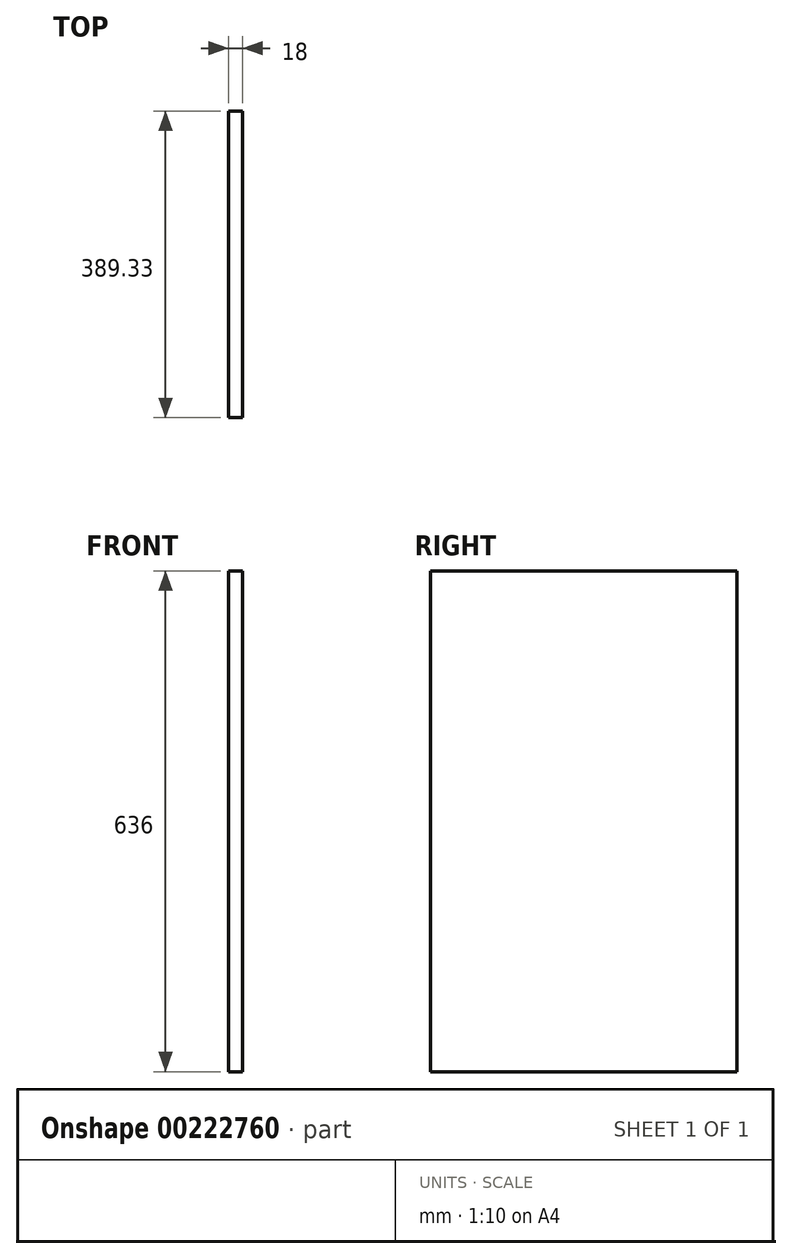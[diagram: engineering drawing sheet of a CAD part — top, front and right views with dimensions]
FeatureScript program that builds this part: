
annotation { "Feature Type Name" : "Feature", "Feature Type Description" : "" }
export const myFeature = defineFeature(function(context is Context, id is Id, definition is map)
    precondition{}
    {
        {
            var Q0;
            Q0=qCreatedBy(makeId("Right.planeOp"),FACE);
            var sketch = newSketch(context, id + "F0", { "sketchPlane" : qUnion([Q0])});
            skLineSegment(sketch, "E0.bottom", {"start": v(0, 0) * mm, "end": v(389.33, 0) * mm});
            skLineSegment(sketch, "E0.top", {"start": v(0, 636) * mm, "end": v(389.33, 636) * mm});
            skLineSegment(sketch, "E0.left", {"start": v(0, 0) * mm, "end": v(0, 636) * mm});
            skLineSegment(sketch, "E0.right", {"start": v(389.33, 0) * mm, "end": v(389.33, 636) * mm});
            skSolve(sketch);
        }
        {
            var Q0;
            Q0=makeQuery(id+"F0.imprint","IMPRINT",FACE,{"disambiguationData":[TD([[makeQuery(id+"F0.imprint","IMPRINT",EDGE,{"derivedFrom":sQuery(id+"F0.wireOp",EDGE,"E0.bottom")}),1.0]])]});
            extrude(context, id + "F1", {"entities" : qUnion([Q0]), "depth" : 18 * mm});
        }
    });
